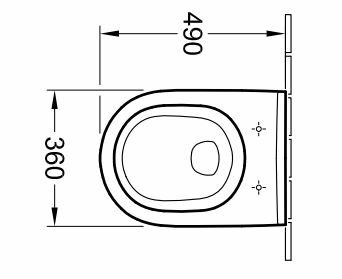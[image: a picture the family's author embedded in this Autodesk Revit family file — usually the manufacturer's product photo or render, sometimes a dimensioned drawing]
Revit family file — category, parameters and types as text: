
# Revit family: Combi-Pack 5656HS
name_source: partatom
category: Plumbing Fixtures
revit_build: Autodesk Revit 2016 (Build: 20150714_1515(x64)
units: mm (PartAtom-declared; Revit-internal decimal feet)

## family parameters
Always vertical = Yes
Cut with Voids When Loaded = No
OmniClass Number = 23.45.00.00
OmniClass Title = Sanitary, Laundry, and Cleaning Equipment
Part Type = Normal
Room Calculation Point = No
Round Connector Dimension = Use Diameter
Shared = No
Work Plane-Based = No

## types (1)
- Combi-Pack 5656HS
    Depth = 530 mm  [stored 1.73885 ft]
    Height = 400 mm  [stored 1.31234 ft]
    Manufacturer = Villeroy and Boch
    Material = Ceramic White
    Model = Combi-Pack 5656HS
    URL = https://pro.villeroy-boch.com
    Width = 370 mm  [stored 1.21391 ft]

note: [stored X ft] marks values corroborated as IEEE doubles in the binary element streams (Revit-internal decimal feet)

## geometry (parser evidence)
native form markers: Sweep x3
no freeform markers — native parametric forms only
